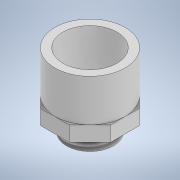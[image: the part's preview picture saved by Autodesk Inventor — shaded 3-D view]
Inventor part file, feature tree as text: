
AUTODESK INVENTOR PART (.ipt)
format: ipt  version: 2022 (Build 260153000, 153)  size: 167,424 bytes
history: native  units: mm
features: extrude x7, sketch x7, other x1, plane x1, thread x1
ambient origin geometry x8: Origin, YZ Plane, XZ Plane, XY Plane, X Axis, Y Axis, Z Axis, Center Point
bodies: Body1 (feature_tree)
feature tree (17):
  other  "Sólido1"
  extrude  "Extrusión1"  Depth=27.76mm
  extrude  "Extrusión2"  Depth=22.6mm
  plane  "Plano de trabajo2"
  extrude  "Extrusión4"  Depth=5.75mm
  extrude  "Extrusión5"  Depth=5.75mm
  extrude  "Extrusión6"  Depth=5.75mm
  extrude  "Extrusión7"  Depth=5.97mm TaperAngle=0.0deg
  thread  "Rosca2"  [1 undecoded]
  extrude  "Extrusión8"  Depth=18.97mm TaperAngle=0.0deg
  sketch  "Boceto1"  dims[d0=21.4mm d1=27.76mm]
  sketch  "Boceto2"  dims[d2=22.6mm d3=0.0mm d5=5.75mm]
  sketch  "Boceto4"  dims[d6=5.75mm d7=5.75mm]
  sketch  "Boceto5"  dims[d8=5.75mm d9=5.75mm]
  sketch  "Boceto6"  dims[d10=5.75mm d11=5.75mm]
  sketch  "Boceto7"  dims[d12=5.75mm d13=5.97mm d14=0.0mm d17=-18.5mm]
  sketch  "Boceto9"  dims[d18=13.6mm d19=18.97mm d20=0.0mm d21=18.97mm d22=0.0mm d25=13.4mm d26=18.6mm d27=18.97mm d28=0.0mm d29=13.6mm d30=18.97mm d31=0.0mm d32=14.87mm d33=0.0mm d34=8.47mm d35=0.0mm]
note: 1 required parameter value undecoded (feature->parameter linkage not recoverable at this tier; creation-order binding heuristic only, values carry confidence <= 0.55)
